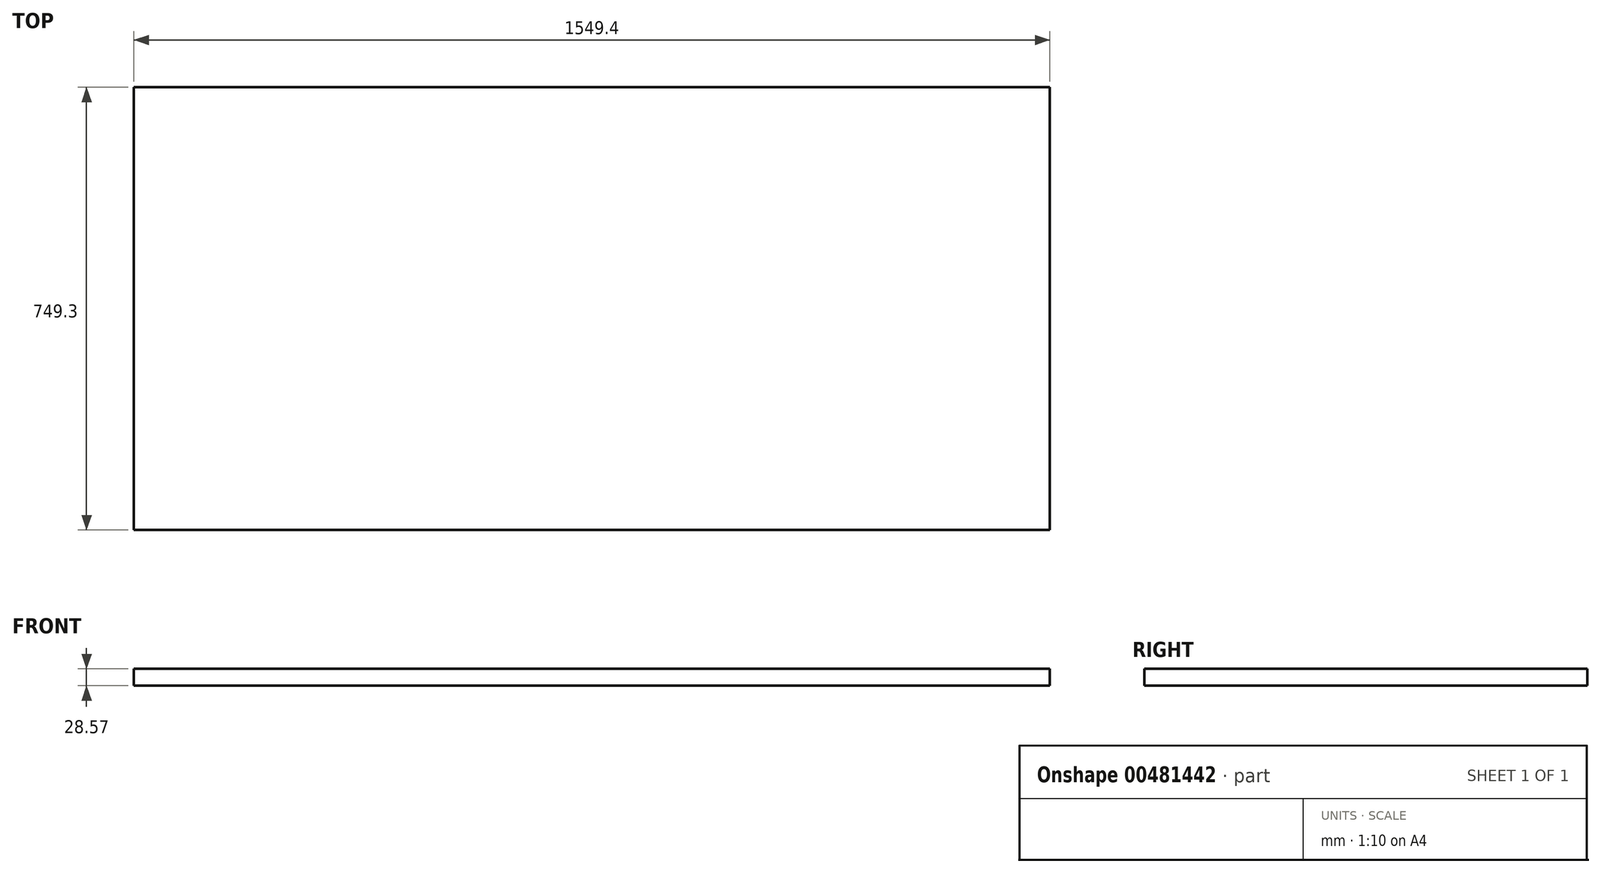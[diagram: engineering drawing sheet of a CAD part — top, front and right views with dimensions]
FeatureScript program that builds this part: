
annotation { "Feature Type Name" : "Feature", "Feature Type Description" : "" }
export const myFeature = defineFeature(function(context is Context, id is Id, definition is map)
    precondition{}
    {
        {
            var Q0;
            Q0=qCreatedBy(makeId("Top.planeOp"),FACE);
            var sketch = newSketch(context, id + "F0", { "sketchPlane" : qUnion([Q0])});
            skLineSegment(sketch, "E0.bottom", {"start": v(-774.7, -374.65) * mm, "end": v(774.7, -374.65) * mm});
            skLineSegment(sketch, "E0.top", {"start": v(-774.7, 374.65) * mm, "end": v(774.7, 374.65) * mm});
            skLineSegment(sketch, "E0.left", {"start": v(-774.7, -374.65) * mm, "end": v(-774.7, 374.65) * mm});
            skLineSegment(sketch, "E0.right", {"start": v(774.7, -374.65) * mm, "end": v(774.7, 374.65) * mm});
            skPoint(sketch, "E0.middle", {"position": v(0, 0) * mm});
            skSolve(sketch);
        }
        {
            var Q0;
            Q0=makeQuery(id+"F0.imprint","IMPRINT",FACE,{"disambiguationData":[TD([[makeQuery(id+"F0.imprint","IMPRINT",EDGE,{"derivedFrom":sQuery(id+"F0.wireOp",EDGE,"E0.bottom")}),1.0]])]});
            extrude(context, id + "F1", {"entities" : qUnion([Q0]), "oppositeDirection" : true, "depth" : 28.57 * mm});
        }
        {
            var Q0;
            Q0=makeQuery(id+"F1.opExtrude","CAP_FACE",FACE,{"disambiguationData":[OSD([sQuery(id+"F0.wireOp",EDGE,"E0.bottom"),sQuery(id+"F0.wireOp",EDGE,"E0.top"),sQuery(id+"F0.wireOp",EDGE,"E0.left"),sQuery(id+"F0.wireOp",EDGE,"E0.right")])],"isStart":false});
            var sketch = newSketch(context, id + "F2", { "sketchPlane" : qUnion([Q0])});
            skLineSegment(sketch, "E1.bottom", {"start": v(-749.3, -349.25) * mm, "end": v(749.3, -349.25) * mm, "construction": true});
            skLineSegment(sketch, "E1.top", {"start": v(-749.3, 349.25) * mm, "end": v(749.3, 349.25) * mm, "construction": true});
            skLineSegment(sketch, "E1.left", {"start": v(-749.3, -349.25) * mm, "end": v(-749.3, 349.25) * mm, "construction": true});
            skLineSegment(sketch, "E1.right", {"start": v(749.3, -349.25) * mm, "end": v(749.3, 349.25) * mm, "construction": true});
            skPoint(sketch, "E1.middle", {"position": v(0, 0) * mm});
            skCircle(sketch, "E2", {"center": v(-749.3, -349.25) * mm, "radius": 13.34 * mm});
            skCircle(sketch, "E3.0.1.0", {"center": v(-749.3, 349.25) * mm, "radius": 13.34 * mm});
            skCircle(sketch, "E3.1.0.0", {"center": v(749.3, -349.25) * mm, "radius": 13.34 * mm});
            skCircle(sketch, "E3.1.1.0", {"center": v(749.3, 349.25) * mm, "radius": 13.34 * mm});
            skCircle(sketch, "E4.1.0.0", {"center": v(-393.7, 349.25) * mm, "radius": 13.34 * mm});
            skCircle(sketch, "E4.1.1.0", {"center": v(-393.7, -349.25) * mm, "radius": 13.34 * mm});
            skLineSegment(sketch, "E4.direction1", {"start": v(-749.3, 349.25) * mm, "end": v(-393.7, 349.25) * mm, "construction": true});
            skLineSegment(sketch, "E4.direction2", {"start": v(-749.3, 349.25) * mm, "end": v(-749.3, -349.25) * mm, "construction": true});
            skLineSegment(sketch, "E5", {"start": v(-393.7, 349.25) * mm, "end": v(165.1, 349.25) * mm});
            skLineSegment(sketch, "E6.direction1", {"start": v(-393.7, 349.25) * mm, "end": v(165.1, 349.25) * mm, "construction": true});
            skCircle(sketch, "E7.1.0.0", {"center": v(177.8, -349.25) * mm, "radius": 13.34 * mm});
            skLineSegment(sketch, "E7.direction1", {"start": v(-393.7, -349.25) * mm, "end": v(177.8, -349.25) * mm, "construction": true});
            skSolve(sketch);
        }
    });
